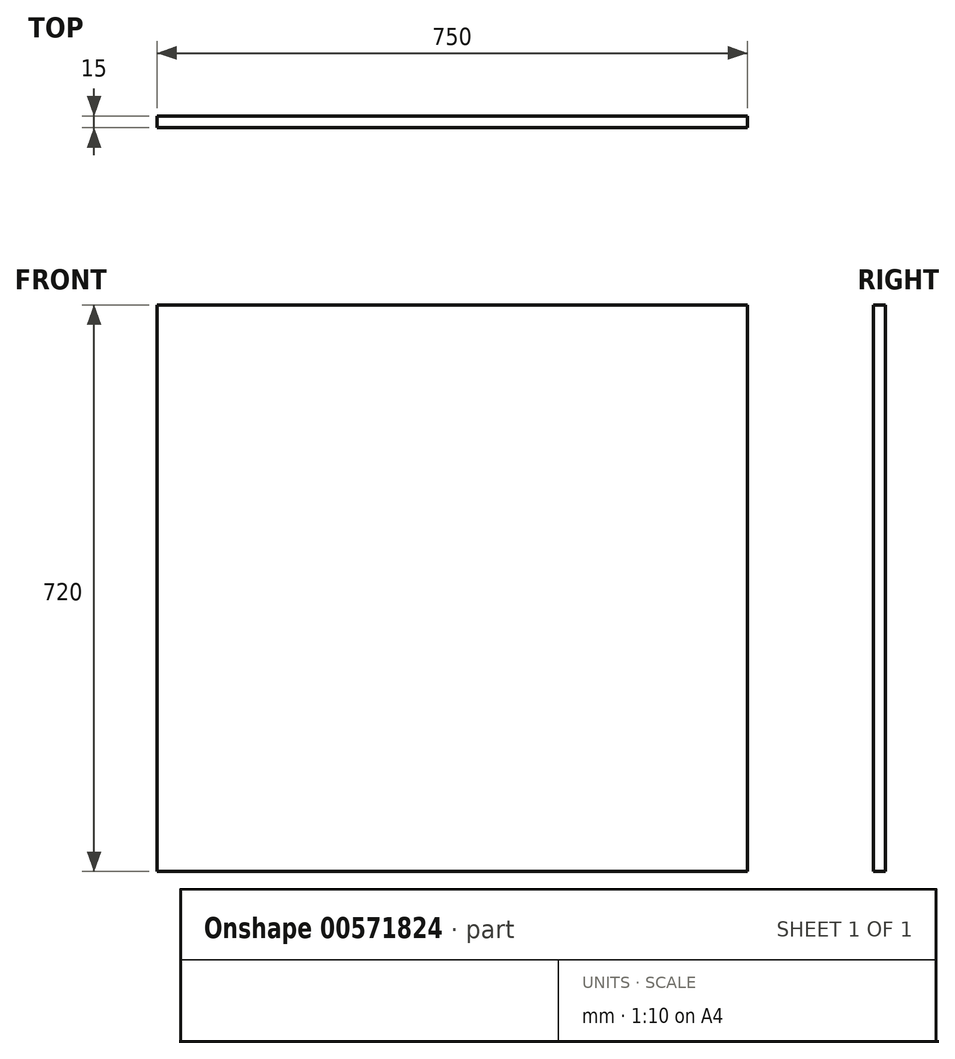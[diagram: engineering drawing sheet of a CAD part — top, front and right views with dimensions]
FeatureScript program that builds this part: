
annotation { "Feature Type Name" : "Feature", "Feature Type Description" : "" }
export const myFeature = defineFeature(function(context is Context, id is Id, definition is map)
    precondition{}
    {
        {
            var Q0;
            Q0=qCreatedBy(makeId("Front.planeOp"),FACE);
            var sketch = newSketch(context, id + "F0", { "sketchPlane" : qUnion([Q0])});
            skLineSegment(sketch, "E0.bottom", {"start": v(-227.93, 377.02) * mm, "end": v(522.07, 377.02) * mm});
            skLineSegment(sketch, "E0.top", {"start": v(-227.93, -342.98) * mm, "end": v(522.07, -342.98) * mm});
            skLineSegment(sketch, "E0.left", {"start": v(-227.93, 377.02) * mm, "end": v(-227.93, -342.98) * mm});
            skLineSegment(sketch, "E0.right", {"start": v(522.07, 377.02) * mm, "end": v(522.07, -342.98) * mm});
            skSolve(sketch);
        }
        {
            var Q0;
            Q0 = qSketchRegion(id + "F0", true);
            extrude(context, id + "F1", {"entities" : qUnion([Q0]), "depth" : 15 * mm, "offsetDistance" : 25 * mm});
        }
    });
